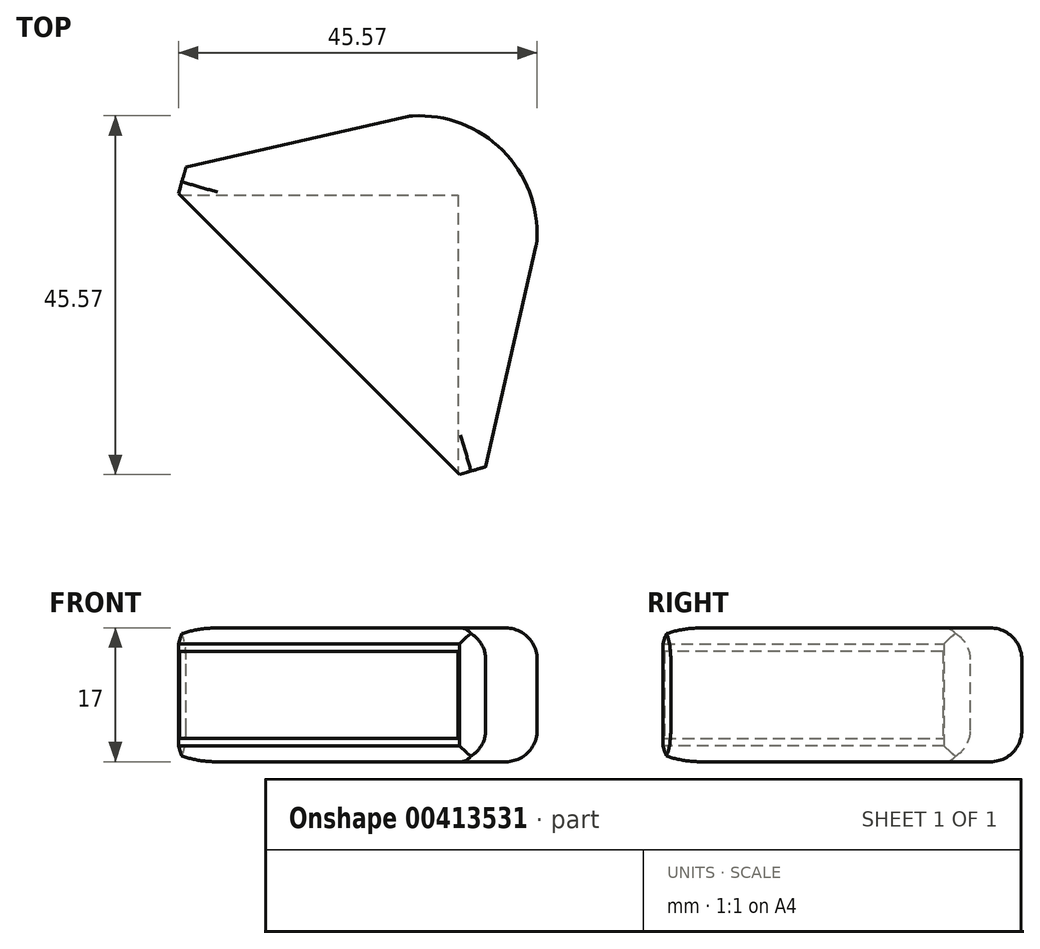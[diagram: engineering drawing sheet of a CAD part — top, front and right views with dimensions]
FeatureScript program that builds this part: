
annotation { "Feature Type Name" : "Feature", "Feature Type Description" : "" }
export const myFeature = defineFeature(function(context is Context, id is Id, definition is map)
    precondition{}
    {
        {
            var Q0;
            Q0=qCreatedBy(makeId("Top.planeOp"),FACE);
            var sketch = newSketch(context, id + "F0", { "sketchPlane" : qUnion([Q0])});
            skLineSegment(sketch, "E0", {"start": v(-50, 0) * mm, "end": v(0, 0) * mm});
            skLineSegment(sketch, "E1", {"start": v(0, 0) * mm, "end": v(0, -50) * mm});
            skLineSegment(sketch, "E2", {"start": v(0, 0) * mm, "end": v(-4.95, -4.95) * mm, "construction": true});
            skCircle(sketch, "E3", {"center": v(-4.95, -4.95) * mm, "radius": 15 * mm});
            skLineSegment(sketch, "E4", {"start": v(10, -6.13) * mm, "end": v(0, -50) * mm});
            skLineSegment(sketch, "E5", {"start": v(-6.13, 10) * mm, "end": v(-50, 0) * mm});
            skLineSegment(sketch, "E6", {"start": v(-38.07, 2.72) * mm, "end": v(2.72, -38.07) * mm});
            skSolve(sketch);
        }
        {
            var Q0;
            {var subQ2=sQuery(id+"F0.wireOp",EDGE,"E0");var subQ5=sQuery(id+"F0.wireOp",EDGE,"E1");var subQ7=makeQuery(id+"F0.imprint","INTERSECT",VERTEX,{"derivedFrom":[subQ2,subQ5]});Q0=makeQuery(id+"F0.imprint","IMPRINT",FACE,{"disambiguationData":[TD([[makeQuery(id+"F0.imprint","IMPRINT",EDGE,{"disambiguationData":[TD([[subQ7,1.0]])],"derivedFrom":subQ2}),1.0]])]});}
            var Q1;
            {var subQ0=sQuery(id+"F0.wireOp",EDGE,"E6");var subQ1=sQuery(id+"F0.wireOp",EDGE,"E1");var subQ2=makeQuery(id+"F0.imprint","INTERSECT",VERTEX,{"derivedFrom":[subQ1,subQ0]});Q1=makeQuery(id+"F0.imprint","IMPRINT",FACE,{"disambiguationData":[TD([[makeQuery(id+"F0.imprint","IMPRINT",EDGE,{"disambiguationData":[TD([[subQ2,1.0]])],"derivedFrom":subQ1}),1.0]])]});}
            var Q2;
            {var subQ0=sQuery(id+"F0.wireOp",EDGE,"E6");var subQ1=sQuery(id+"F0.wireOp",EDGE,"E0");var subQ2=makeQuery(id+"F0.imprint","INTERSECT",VERTEX,{"derivedFrom":[subQ1,subQ0]});Q2=makeQuery(id+"F0.imprint","IMPRINT",FACE,{"disambiguationData":[TD([[makeQuery(id+"F0.imprint","IMPRINT",EDGE,{"disambiguationData":[TD([[subQ2,-1.0]])],"derivedFrom":subQ1}),1.0]])]});}
            var Q3;
            {var subQ0=sQuery(id+"F0.wireOp",EDGE,"E6");var subQ1=sQuery(id+"F0.wireOp",EDGE,"E0");var subQ2=makeQuery(id+"F0.imprint","INTERSECT",VERTEX,{"derivedFrom":[subQ1,subQ0]});Q3=makeQuery(id+"F0.imprint","IMPRINT",FACE,{"disambiguationData":[TD([[makeQuery(id+"F0.imprint","IMPRINT",EDGE,{"disambiguationData":[TD([[subQ2,-1.0]])],"derivedFrom":subQ1}),-1.0]])]});}
            var Q4;
            {var subQ0=sQuery(id+"F0.wireOp",EDGE,"E1");var subQ1=sQuery(id+"F0.wireOp",EDGE,"E0");var subQ2=makeQuery(id+"F0.imprint","INTERSECT",VERTEX,{"derivedFrom":[subQ1,subQ0]});Q4=makeQuery(id+"F0.imprint","IMPRINT",FACE,{"disambiguationData":[TD([[makeQuery(id+"F0.imprint","IMPRINT",EDGE,{"disambiguationData":[TD([[subQ2,1.0]])],"derivedFrom":subQ1}),-1.0]])]});}
            extrude(context, id + "F1", {"entities" : qUnion([Q0, Q1, Q2, Q3, Q4]), "depth" : 3 * mm});
        }
        {
            var Q0;
            {var subQ0=sQuery(id+"F0.wireOp",EDGE,"E6");var subQ1=sQuery(id+"F0.wireOp",EDGE,"E1");var subQ2=makeQuery(id+"F0.imprint","INTERSECT",VERTEX,{"derivedFrom":[subQ1,subQ0]});Q0=makeQuery(id+"F0.imprint","IMPRINT",FACE,{"disambiguationData":[TD([[makeQuery(id+"F0.imprint","IMPRINT",EDGE,{"disambiguationData":[TD([[subQ2,1.0]])],"derivedFrom":subQ1}),1.0]])]});}
            var Q1;
            {var subQ2=sQuery(id+"F0.wireOp",EDGE,"E0");var subQ5=sQuery(id+"F0.wireOp",EDGE,"E1");var subQ7=makeQuery(id+"F0.imprint","INTERSECT",VERTEX,{"derivedFrom":[subQ2,subQ5]});Q1=makeQuery(id+"F0.imprint","IMPRINT",FACE,{"disambiguationData":[TD([[makeQuery(id+"F0.imprint","IMPRINT",EDGE,{"disambiguationData":[TD([[subQ7,1.0]])],"derivedFrom":subQ2}),1.0]])]});}
            var Q2;
            {var subQ0=sQuery(id+"F0.wireOp",EDGE,"E6");var subQ1=sQuery(id+"F0.wireOp",EDGE,"E0");var subQ2=makeQuery(id+"F0.imprint","INTERSECT",VERTEX,{"derivedFrom":[subQ1,subQ0]});Q2=makeQuery(id+"F0.imprint","IMPRINT",FACE,{"disambiguationData":[TD([[makeQuery(id+"F0.imprint","IMPRINT",EDGE,{"disambiguationData":[TD([[subQ2,-1.0]])],"derivedFrom":subQ1}),1.0]])]});}
            extrude(context, id + "F2", {"entities" : qUnion([Q0, Q1, Q2]), "operationType" : NewBodyOperationType.ADD, "depth" : 16 * mm});
        }
        {
            var Q0;
            {var subQ0=sQuery(id+"F0.wireOp",EDGE,"E6");var subQ1=sQuery(id+"F0.wireOp",EDGE,"E0");var subQ2=makeQuery(id+"F0.imprint","INTERSECT",VERTEX,{"derivedFrom":[subQ1,subQ0]});Q0=makeQuery(id+"F0.imprint","IMPRINT",FACE,{"disambiguationData":[TD([[makeQuery(id+"F0.imprint","IMPRINT",EDGE,{"disambiguationData":[TD([[subQ2,-1.0]])],"derivedFrom":subQ1}),-1.0]])]});}
            var Q1;
            {var subQ0=sQuery(id+"F0.wireOp",EDGE,"E1");var subQ1=sQuery(id+"F0.wireOp",EDGE,"E0");var subQ2=makeQuery(id+"F0.imprint","INTERSECT",VERTEX,{"derivedFrom":[subQ1,subQ0]});Q1=makeQuery(id+"F0.imprint","IMPRINT",FACE,{"disambiguationData":[TD([[makeQuery(id+"F0.imprint","IMPRINT",EDGE,{"disambiguationData":[TD([[subQ2,1.0]])],"derivedFrom":subQ1}),-1.0]])]});}
            var Q2;
            {var subQ2=sQuery(id+"F0.wireOp",EDGE,"E0");var subQ5=sQuery(id+"F0.wireOp",EDGE,"E1");var subQ7=makeQuery(id+"F0.imprint","INTERSECT",VERTEX,{"derivedFrom":[subQ2,subQ5]});Q2=makeQuery(id+"F0.imprint","IMPRINT",FACE,{"disambiguationData":[TD([[makeQuery(id+"F0.imprint","IMPRINT",EDGE,{"disambiguationData":[TD([[subQ7,1.0]])],"derivedFrom":subQ2}),1.0]])]});}
            var Q3;
            {var subQ0=sQuery(id+"F0.wireOp",EDGE,"E6");var subQ1=sQuery(id+"F0.wireOp",EDGE,"E1");var subQ2=makeQuery(id+"F0.imprint","INTERSECT",VERTEX,{"derivedFrom":[subQ1,subQ0]});Q3=makeQuery(id+"F0.imprint","IMPRINT",FACE,{"disambiguationData":[TD([[makeQuery(id+"F0.imprint","IMPRINT",EDGE,{"disambiguationData":[TD([[subQ2,1.0]])],"derivedFrom":subQ1}),1.0]])]});}
            var Q4;
            {var subQ0=sQuery(id+"F0.wireOp",EDGE,"E6");var subQ1=sQuery(id+"F0.wireOp",EDGE,"E0");var subQ2=makeQuery(id+"F0.imprint","INTERSECT",VERTEX,{"derivedFrom":[subQ1,subQ0]});Q4=makeQuery(id+"F0.imprint","IMPRINT",FACE,{"disambiguationData":[TD([[makeQuery(id+"F0.imprint","IMPRINT",EDGE,{"disambiguationData":[TD([[subQ2,-1.0]])],"derivedFrom":subQ1}),1.0]])]});}
            extrude(context, id + "F3", {"entities" : qUnion([Q0, Q1, Q2, Q3, Q4]), "operationType" : NewBodyOperationType.ADD, "depth" : 17 * mm, "hasSecondDirection" : true, "secondDirectionOppositeDirection" : true, "secondDirectionDepth" : -14 * mm});
        }
        {
            var Q0;
            {var subQ0=sQuery(id+"F0.wireOp",EDGE,"E6");var subQ1=sQuery(id+"F0.wireOp",EDGE,"E5");Q0=makeQuery(id+"F3.boolean.opBoolean","MERGE",EDGE,{"derivedFrom":[makeQuery(id+"F2.boolean.opBoolean","MERGE",EDGE,{"derivedFrom":[makeQuery(id+"F1.opExtrude","SWEPT_EDGE",EDGE,{"disambiguationData":[OSD([subQ1,subQ0])]}),makeQuery(id+"F2.opExtrude","SWEPT_EDGE",EDGE,{"disambiguationData":[OSD([subQ1,subQ0])]})]}),makeQuery(id+"F3.opExtrude","SWEPT_EDGE",EDGE,{"disambiguationData":[OSD([subQ1,subQ0])]})]});}
            var Q1;
            {var subQ0=sQuery(id+"F0.wireOp",EDGE,"E6");var subQ1=sQuery(id+"F0.wireOp",EDGE,"E4");Q1=makeQuery(id+"F3.boolean.opBoolean","MERGE",EDGE,{"derivedFrom":[makeQuery(id+"F2.boolean.opBoolean","MERGE",EDGE,{"derivedFrom":[makeQuery(id+"F1.opExtrude","SWEPT_EDGE",EDGE,{"disambiguationData":[OSD([subQ1,subQ0])]}),makeQuery(id+"F2.opExtrude","SWEPT_EDGE",EDGE,{"disambiguationData":[OSD([subQ1,subQ0])]})]}),makeQuery(id+"F3.opExtrude","SWEPT_EDGE",EDGE,{"disambiguationData":[OSD([subQ1,subQ0])]})]});}
            var Q2;
            Q2=makeQuery(id+"F3.opExtrude","CAP_EDGE",EDGE,{"disambiguationData":[OSD([sQuery(id+"F0.wireOp",EDGE,"E6")])],"isStart":false});
            var Q3;
            Q3=makeQuery(id+"F1.opExtrude","CAP_EDGE",EDGE,{"disambiguationData":[OSD([sQuery(id+"F0.wireOp",EDGE,"E6")])],"isStart":true});
            chamfer(context, id + "F4", {"entities" : qUnion([Q0, Q1, Q2, Q3]), "width" : 2 * mm, "tangentPropagation" : true});
        }
        {
            var Q0;
            Q0=makeQuery(id+"F3.opExtrude","CAP_FACE",FACE,{"disambiguationData":[OSD([sQuery(id+"F0.wireOp",EDGE,"E3"),sQuery(id+"F0.wireOp",EDGE,"E4"),sQuery(id+"F0.wireOp",EDGE,"E5"),sQuery(id+"F0.wireOp",EDGE,"E6")])],"isStart":false});
            var Q1;
            Q1=makeQuery(id+"F1.opExtrude","CAP_FACE",FACE,{"disambiguationData":[OSD([sQuery(id+"F0.wireOp",EDGE,"E3"),sQuery(id+"F0.wireOp",EDGE,"E4"),sQuery(id+"F0.wireOp",EDGE,"E5"),sQuery(id+"F0.wireOp",EDGE,"E6")])],"isStart":true});
            var Q2;
            {var subQ0=sQuery(id+"F0.wireOp",EDGE,"E5");var subQ1=sQuery(id+"F0.wireOp",EDGE,"E3");Q2=makeQuery(id+"F3.boolean.opBoolean","MERGE",EDGE,{"derivedFrom":[makeQuery(id+"F2.boolean.opBoolean","MERGE",EDGE,{"derivedFrom":[makeQuery(id+"F1.opExtrude","SWEPT_EDGE",EDGE,{"disambiguationData":[OSD([subQ1,subQ0])]}),makeQuery(id+"F2.opExtrude","SWEPT_EDGE",EDGE,{"disambiguationData":[OSD([subQ1,subQ0])]})]}),makeQuery(id+"F3.opExtrude","SWEPT_EDGE",EDGE,{"disambiguationData":[OSD([subQ1,subQ0])]})]});}
            var Q3;
            {var subQ0=sQuery(id+"F0.wireOp",EDGE,"E4");var subQ1=sQuery(id+"F0.wireOp",EDGE,"E3");Q3=makeQuery(id+"F3.boolean.opBoolean","MERGE",EDGE,{"derivedFrom":[makeQuery(id+"F2.boolean.opBoolean","MERGE",EDGE,{"derivedFrom":[makeQuery(id+"F1.opExtrude","SWEPT_EDGE",EDGE,{"disambiguationData":[OSD([subQ1,subQ0])]}),makeQuery(id+"F2.opExtrude","SWEPT_EDGE",EDGE,{"disambiguationData":[OSD([subQ1,subQ0])]})]}),makeQuery(id+"F3.opExtrude","SWEPT_EDGE",EDGE,{"disambiguationData":[OSD([subQ1,subQ0])]})]});}
            fillet(context, id + "F5", {"entities" : qUnion([Q0, Q1, Q2, Q3]), "radius" : 4 * mm, "tangentPropagation" : true, "allowEdgeOverflow" : false});
        }
    });
